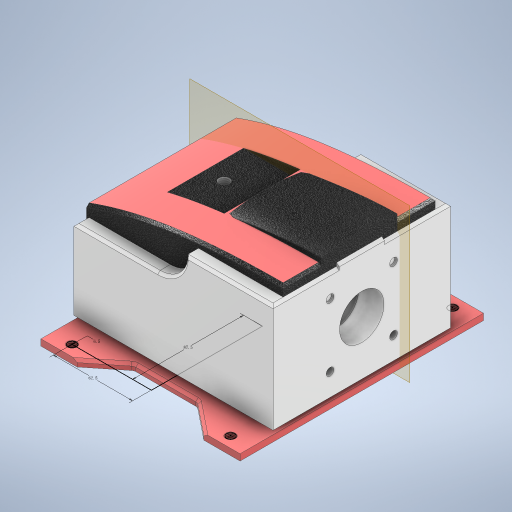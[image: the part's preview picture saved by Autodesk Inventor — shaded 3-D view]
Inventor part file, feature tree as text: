
AUTODESK INVENTOR PART (.ipt)
format: ipt  version: 2023.5 (Build 275446000, 446)  size: 547,328 bytes
history: native  units: mm
features: sketch x14, extrude x10, chamfer x4, thread x4, hole x2, mirror x2, plane x1, sweep x1, fillet x1
ambient origin geometry x8: Origin, YZ Plane, XZ Plane, XY Plane, X Axis, Y Axis, Z Axis, Center Point
bodies: 实体1 (feature_tree)
feature tree (39):
  extrude  "拉伸1"  Depth=192.0mm
  sketch  "草图2"  dims[d2=5.0mm d3=0.0mm d4=87.5mm]
  extrude  "拉伸2"  Depth=5.0mm
  extrude  "拉伸3"  Depth=60.0mm
  extrude  "拉伸4"  Depth=3.0mm
  hole  "孔2"  [1 undecoded]
  extrude  "拉伸5"  Depth=20.0mm
  mirror  "镜像1"
  extrude  "拉伸7"  Depth=10.0mm TaperAngle=0.0deg
  chamfer  "倒角3"  Distance=120.0mm
  extrude  "拉伸8"  Depth=8.0mm
  hole  "孔3"  [1 undecoded]
  extrude  "拉伸9"  Depth=5.0mm TaperAngle=0.0deg
  chamfer  "倒角4"  Distance=2.0mm Angle=45.0deg
  sketch  "草图13"  dims[d49=2.0mm d50=2.0mm d51=45.0deg d52=8.0mm]
  plane  "工作平面1"
  sweep  "扫掠1"
  extrude  "拉伸10"  Depth=8.0mm
  mirror  "镜像2"
  fillet  "圆角1"  Radius=8.0mm
  chamfer  "倒角5"  Angle=90.0deg  [1 undecoded]
  extrude  "拉伸11"  TaperAngle=0.0deg  [1 undecoded]
  thread  "螺纹1"  [1 undecoded]
  thread  "螺纹2"  [1 undecoded]
  thread  "螺纹3"  [1 undecoded]
  thread  "螺纹4"  [1 undecoded]
  chamfer  "倒角6"  Distance=4.0mm
  sketch  "草图1"  dims[d0=157.0mm d1=192.0mm]
  sketch  "草图3"  dims[d6=62.5mm d14=60.0mm]
  sketch  "草图4"  dims[d15=3.0mm d16=0.0mm d17=140.0mm]
  sketch  "草图5"  dims[d18=85.0mm d19=0.0mm d20=35.0mm]
  sketch  "草图6"  dims[d21=20.0mm d22=0.0mm d23=50.0mm]
  sketch  "草图7"  dims[d24=50.0mm]
  sketch  "草图9"  dims[d25=6.0mm d26=12.0mm d27=4.0mm d28=2.0mm d29=90.0deg d30=10.0mm d31=20.594885mm d32=70.0mm d33=0.0mm]
  sketch  "草图10"  dims[d44=155.0mm]
  sketch  "草图11"  dims[d45=30.0mm]
  sketch  "草图12"  dims[d46=8.0mm d47=120.0mm d48=0.0mm]
  sketch  "草图14"  dims[d53=60.0mm d54=61.75mm d55=54.25mm d56=0.0mm d57=0.0mm]
  sketch  "草图16"  dims[d58=10.0mm d59=8.376mm d60=20.0mm d61=4.0mm d62=2.0mm d63=90.0deg d64=10.0mm d65=20.594885mm d66=27.0mm d67=0.0mm d68=2.0mm d69=2.0mm d70=45.0deg d71=60.0mm d72=8.0mm d73=8.0mm d74=90.0deg d75=0.0mm d76=0.0mm d77=100.0mm d78=50.0mm d79=20.0mm d80=27.0mm d81=0.0mm d82=4.0mm d83=2.0mm d84=2.0mm d85=45.0deg d86=6.5mm d87=10.0mm d88=0.0mm d89=5.0mm d90=0.0mm d91=5.0mm d92=0.0mm d93=5.0mm d94=0.0mm d95=5.0mm d96=0.0mm d97=0.5mm d98=2.0mm d99=45.0deg]
note: 8 required parameter values undecoded (feature->parameter linkage not recoverable at this tier; creation-order binding heuristic only, values carry confidence <= 0.55)
